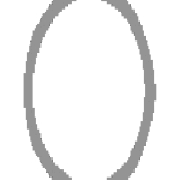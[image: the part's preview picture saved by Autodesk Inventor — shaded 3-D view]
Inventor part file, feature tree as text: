
AUTODESK INVENTOR PART (.ipt)
format: ipt  version: 2021 (Build 250183000, 183)  size: 109,568 bytes
history: native  units: in
note: dims shown in document units (in); Inventor stores cm internally (conversion verified against a paired STEP export)
features: other x4, sketch x3, plane x1
ambient origin geometry x8: Origin, YZ Plane, XZ Plane, XY Plane, X Axis, Y Axis, Z Axis, Center Point
bodies: Solid1 (feature_tree), Body (feature_tree)
feature tree (8):
  other  "Driven Length"
  other  "Frame Generator"
  other  "Start Plane"
  other  "End Plane"
  sketch  "Sketch"  dims[d2=20.0in d4=-0.0in d5=20.0in d6=0.12in d7=0.0in d10=90.0deg d9=20.0in]
  sketch  "Sketch4"  dims[d0=1.0in]
  plane  "Work Plane4"
  sketch  "Sketch5"  dims[d1=0.065in]
